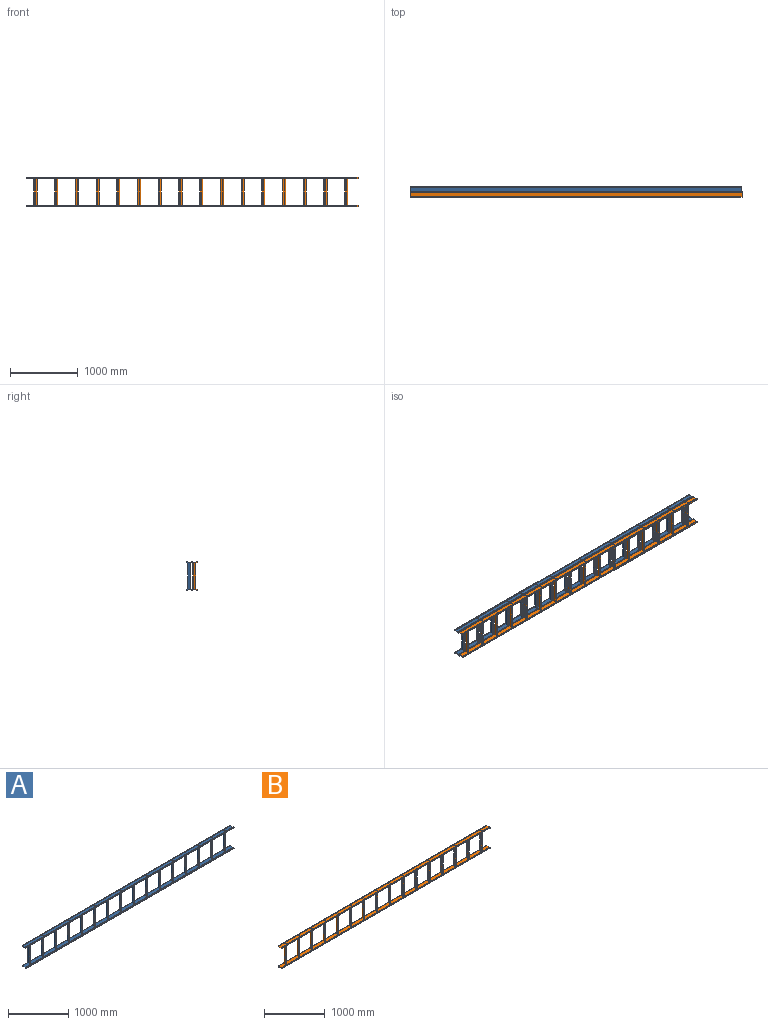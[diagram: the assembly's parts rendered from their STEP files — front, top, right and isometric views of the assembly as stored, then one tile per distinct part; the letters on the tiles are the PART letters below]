
ASSEMBLY  parts=2 mates=1
PART A: 108 faces, bbox 4876.8x88.6x440.7 mm
  f0: plane 4876.8x69.85mm, normal (0,0,1), area 321795mm2, adj f17,f18,f20,f42,f43,f44,f45,f46
  f1: plane 4876.8x22.23mm, normal (0,-1,0), area 108386.9mm2, adj f2,f19,f20,f102
  f2: plane 4876.8x7.46mm, normal (0,0,1), area 36387mm2, adj f1,f3,f20,f102
  f3: plane 4876.8x3.97mm, normal (0,1,0), area 19354.8mm2, adj f2,f4,f20,f102
  f4: plane 4876.8x3.18mm, normal (0,0,-1), area 15483.8mm2, adj f3,f5,f20,f102
  f5: plane 4876.8x2.38mm, normal (0,1,0), area 11612.9mm2, adj f4,f6,f20,f102
  f6: plane 4876.8x5.56mm, normal (0,0,1), area 27096.7mm2, adj f5,f7,f20,f102
  f7: plane 4876.8x10.8mm, normal (0,-1,0), area 52645.1mm2, adj f6,f8,f20,f102
  f8: plane 4876.8x14.29mm, normal (0,0,-1), area 69677.3mm2, adj f7,f9,f20,f102
  f9: plane 4876.8x16.72mm, normal (0,1,0), area 81548.1mm2, adj f8,f10,f20,f102
  f10: plane 4876.8x69.85mm, normal (0,0,-1), area 340644.5mm2, adj f9,f11,f20,f102
  f11: plane 4876.8x9.1mm, normal (0,-1,0), area 44386.8mm2, adj f10,f12,f20,f102
  f12: plane 4876.8x2.38mm, normal (0,0,1), area 11612.9mm2, adj f11,f13,f20,f102
  f13: plane 4876.8x3.18mm, normal (0,-1,0), area 15483.8mm2, adj f12,f14,f20,f102
  f14: plane 4876.8x6.83mm, normal (0,0,-1), area 33290.3mm2, adj f13,f15,f20,f102
  f15: plane 4876.8x22.23mm, normal (0,1,0), area 108386.9mm2, adj f14,f16,f20,f102
  f16: plane 4876.8x4.45mm, normal (0,0,1), area 21677.4mm2, adj f15,f17,f20,f102
  f17: plane 4876.8x3.18mm, normal (0,-1,0), area 15483.8mm2, adj f0,f16,f20,f102
  f18: plane 4876.8x3.18mm, normal (0,1,0), area 15483.8mm2, adj f0,f19,f20,f102
  f19: plane 4876.8x4.45mm, normal (0,0,1), area 21677.4mm2, adj f1,f18,f20,f102
  f20: plane 88.58x26.67mm, normal (-1,0,0), area 764.4mm2, adj f0,f1,f2,f3,f4,f5,f6,f7
  f21: plane 4876.8x69.85mm, normal (0,0,-1), area 321795mm2, adj f33,f34,f41,f42,f43,f44,f45,f46
  f22: plane 4876.8x69.85mm, normal (0,0,1), area 340644.5mm2, adj f23,f40,f41,f103
  f23: plane 4876.8x16.72mm, normal (0,1,0), area 81548.1mm2, adj f22,f24,f41,f103
  f24: plane 4876.8x14.29mm, normal (0,0,1), area 69677.3mm2, adj f23,f25,f41,f103
  f25: plane 4876.8x10.8mm, normal (0,-1,0), area 52645.1mm2, adj f24,f26,f41,f103
  f26: plane 4876.8x5.56mm, normal (0,0,-1), area 27096.7mm2, adj f25,f27,f41,f103
  f27: plane 4876.8x2.38mm, normal (0,1,0), area 11612.9mm2, adj f26,f28,f41,f103
  f28: plane 4876.8x3.18mm, normal (0,0,1), area 15483.8mm2, adj f27,f29,f41,f103
  f29: plane 4876.8x3.97mm, normal (0,1,0), area 19354.8mm2, adj f28,f30,f41,f103
  f30: plane 4876.8x7.46mm, normal (0,0,-1), area 36387mm2, adj f29,f31,f41,f103
  f31: plane 4876.8x22.23mm, normal (0,-1,0), area 108386.9mm2, adj f30,f32,f41,f103
  f32: plane 4876.8x4.45mm, normal (0,0,-1), area 21677.4mm2, adj f31,f33,f41,f103
  f33: plane 4876.8x3.18mm, normal (0,1,0), area 15483.8mm2, adj f21,f32,f41,f103
  f34: plane 4876.8x3.18mm, normal (0,-1,0), area 15483.8mm2, adj f21,f35,f41,f103
  f35: plane 4876.8x4.45mm, normal (0,0,-1), area 21677.4mm2, adj f34,f36,f41,f103
  f36: plane 4876.8x22.23mm, normal (0,1,0), area 108386.9mm2, adj f35,f37,f41,f103
  f37: plane 4876.8x6.83mm, normal (0,0,1), area 33290.3mm2, adj f36,f38,f41,f103
  f38: plane 4876.8x3.18mm, normal (0,-1,0), area 15483.8mm2, adj f37,f39,f41,f103
  f39: plane 4876.8x2.38mm, normal (0,0,-1), area 11612.9mm2, adj f38,f40,f41,f103
  f40: plane 4876.8x9.1mm, normal (0,-1,0), area 44386.8mm2, adj f22,f39,f41,f103
  f41: plane 88.58x26.67mm, normal (-1,0,0), area 764.4mm2, adj f21,f22,f23,f24,f25,f26,f27,f28
  f42: plane 393.7x18.97mm, normal (0,-1,0), area 7469.5mm2, adj f0,f21,f43,f44
  f43: plane 393.7x43.18mm, normal (-0.97,0.26,0), area 17599.7mm2, adj f0,f21,f42,f45
  f44: cylinder r=17.46mm len=393.7mm, axis (0,0,-1), area 20918.1mm2, adj f0,f21,f42,f45
  f45: plane 393.7x16.43mm, normal (0.5,0.87,0), area 7469.5mm2, adj f0,f21,f43,f44
  f46: plane 393.7x18.97mm, normal (0,-1,0), area 7469.5mm2, adj f0,f21,f47,f48
  f47: plane 393.7x43.18mm, normal (-0.97,0.26,0), area 17599.7mm2, adj f0,f21,f46,f49
  f48: cylinder r=17.46mm len=393.7mm, axis (0,0,-1), area 20918.1mm2, adj f0,f21,f46,f49
  f49: plane 393.7x16.43mm, normal (0.5,0.87,0), area 7469.5mm2, adj f0,f21,f47,f48
  f50: plane 393.7x18.97mm, normal (0,-1,0), area 7469.5mm2, adj f0,f21,f51,f52
  f51: plane 393.7x43.18mm, normal (-0.97,0.26,0), area 17599.7mm2, adj f0,f21,f50,f53
  f52: cylinder r=17.46mm len=393.7mm, axis (0,0,-1), area 20918.1mm2, adj f0,f21,f50,f53
  f53: plane 393.7x16.43mm, normal (0.5,0.87,0), area 7469.5mm2, adj f0,f21,f51,f52
  f54: plane 393.7x18.97mm, normal (0,-1,0), area 7469.5mm2, adj f0,f21,f55,f56
  f55: plane 393.7x43.18mm, normal (-0.97,0.26,0), area 17599.7mm2, adj f0,f21,f54,f57
  f56: cylinder r=17.46mm len=393.7mm, axis (0,0,-1), area 20918.1mm2, adj f0,f21,f54,f57
  f57: plane 393.7x16.43mm, normal (0.5,0.87,0), area 7469.5mm2, adj f0,f21,f55,f56
  f58: plane 393.7x18.97mm, normal (0,-1,0), area 7469.5mm2, adj f0,f21,f59,f60
  f59: plane 393.7x43.18mm, normal (-0.97,0.26,0), area 17599.7mm2, adj f0,f21,f58,f61
  f60: cylinder r=17.46mm len=393.7mm, axis (0,0,-1), area 20918.1mm2, adj f0,f21,f58,f61
  f61: plane 393.7x16.43mm, normal (0.5,0.87,0), area 7469.5mm2, adj f0,f21,f59,f60
  f62: plane 393.7x18.97mm, normal (0,-1,0), area 7469.5mm2, adj f0,f21,f63,f64
  f63: plane 393.7x43.18mm, normal (-0.97,0.26,0), area 17599.7mm2, adj f0,f21,f62,f65
  f64: cylinder r=17.46mm len=393.7mm, axis (0,0,-1), area 20918.1mm2, adj f0,f21,f62,f65
  f65: plane 393.7x16.43mm, normal (0.5,0.87,0), area 7469.5mm2, adj f0,f21,f63,f64
  f66: plane 393.7x18.97mm, normal (0,-1,0), area 7469.5mm2, adj f0,f21,f67,f68
  f67: plane 393.7x43.18mm, normal (-0.97,0.26,0), area 17599.7mm2, adj f0,f21,f66,f69
  f68: cylinder r=17.46mm len=393.7mm, axis (0,0,-1), area 20918.1mm2, adj f0,f21,f66,f69
  f69: plane 393.7x16.43mm, normal (0.5,0.87,0), area 7469.5mm2, adj f0,f21,f67,f68
  f70: plane 393.7x18.97mm, normal (0,-1,0), area 7469.5mm2, adj f0,f21,f71,f72
  f71: plane 393.7x43.18mm, normal (-0.97,0.26,0), area 17599.7mm2, adj f0,f21,f70,f73
  f72: cylinder r=17.46mm len=393.7mm, axis (0,0,-1), area 20918.1mm2, adj f0,f21,f70,f73
  f73: plane 393.7x16.43mm, normal (0.5,0.87,0), area 7469.5mm2, adj f0,f21,f71,f72
  f74: plane 393.7x18.97mm, normal (0,-1,0), area 7469.5mm2, adj f0,f21,f75,f76
  f75: plane 393.7x43.18mm, normal (-0.97,0.26,0), area 17599.7mm2, adj f0,f21,f74,f77
  f76: cylinder r=17.46mm len=393.7mm, axis (0,0,-1), area 20918.1mm2, adj f0,f21,f74,f77
  f77: plane 393.7x16.43mm, normal (0.5,0.87,0), area 7469.5mm2, adj f0,f21,f75,f76
  f78: plane 393.7x18.97mm, normal (0,-1,0), area 7469.5mm2, adj f0,f21,f79,f80
  f79: plane 393.7x43.18mm, normal (-0.97,0.26,0), area 17599.7mm2, adj f0,f21,f78,f81
  f80: cylinder r=17.46mm len=393.7mm, axis (0,0,-1), area 20918.1mm2, adj f0,f21,f78,f81
  f81: plane 393.7x16.43mm, normal (0.5,0.87,0), area 7469.5mm2, adj f0,f21,f79,f80
  f82: plane 393.7x18.97mm, normal (0,-1,0), area 7469.5mm2, adj f0,f21,f83,f84
  f83: plane 393.7x43.18mm, normal (-0.97,0.26,0), area 17599.7mm2, adj f0,f21,f82,f85
  f84: cylinder r=17.46mm len=393.7mm, axis (0,0,-1), area 20918.1mm2, adj f0,f21,f82,f85
  f85: plane 393.7x16.43mm, normal (0.5,0.87,0), area 7469.5mm2, adj f0,f21,f83,f84
  f86: plane 393.7x18.97mm, normal (0,-1,0), area 7469.5mm2, adj f0,f21,f87,f88
  f87: plane 393.7x43.18mm, normal (-0.97,0.26,0), area 17599.7mm2, adj f0,f21,f86,f89
  f88: cylinder r=17.46mm len=393.7mm, axis (0,0,-1), area 20918.1mm2, adj f0,f21,f86,f89
  f89: plane 393.7x16.43mm, normal (0.5,0.87,0), area 7469.5mm2, adj f0,f21,f87,f88
  f90: plane 393.7x18.97mm, normal (0,-1,0), area 7469.5mm2, adj f0,f21,f91,f92
  f91: plane 393.7x43.18mm, normal (-0.97,0.26,0), area 17599.7mm2, adj f0,f21,f90,f93
  f92: cylinder r=17.46mm len=393.7mm, axis (0,0,-1), area 20918.1mm2, adj f0,f21,f90,f93
  f93: plane 393.7x16.43mm, normal (0.5,0.87,0), area 7469.5mm2, adj f0,f21,f91,f92
  f94: plane 393.7x18.97mm, normal (0,-1,0), area 7469.5mm2, adj f0,f21,f95,f96
  f95: plane 393.7x43.18mm, normal (-0.97,0.26,0), area 17599.7mm2, adj f0,f21,f94,f97
  f96: cylinder r=17.46mm len=393.7mm, axis (0,0,-1), area 20918.1mm2, adj f0,f21,f94,f97
  f97: plane 393.7x16.43mm, normal (0.5,0.87,0), area 7469.5mm2, adj f0,f21,f95,f96
  f98: plane 393.7x18.97mm, normal (0,-1,0), area 7469.5mm2, adj f0,f21,f99,f100
  f99: plane 393.7x43.18mm, normal (-0.97,0.26,0), area 17599.7mm2, adj f0,f21,f98,f101
  f100: cylinder r=17.46mm len=393.7mm, axis (0,0,-1), area 20918.1mm2, adj f0,f21,f98,f101
  f101: plane 393.7x16.43mm, normal (0.5,0.87,0), area 7469.5mm2, adj f0,f21,f99,f100
  f102: plane 88.58x26.67mm, normal (1,0,0), area 764.4mm2, adj f0,f1,f2,f3,f4,f5,f6,f7
  f103: plane 88.58x26.67mm, normal (1,0,0), area 764.4mm2, adj f21,f22,f23,f24,f25,f26,f27,f28
  f104: plane 393.7x18.97mm, normal (0,-1,0), area 7469.5mm2, adj f0,f21,f105,f106
  f105: plane 393.7x43.18mm, normal (-0.97,0.26,0), area 17599.7mm2, adj f0,f21,f104,f107
  f106: cylinder r=17.46mm len=393.7mm, axis (0,0,-1), area 20918.1mm2, adj f0,f21,f104,f107
  f107: plane 393.7x16.43mm, normal (0.5,0.87,0), area 7469.5mm2, adj f0,f21,f105,f106
PART B: 100 faces, bbox 4876.8x78.7x431.8 mm
  f0: plane 4876.8x69.85mm, normal (0,0,1), area 321795mm2, adj f12,f13,f16,f34,f35,f36,f37,f38
  f1: plane 4876.8x7.62mm, normal (0,0,-1), area 37161.2mm2, adj f2,f15,f16,f94
  f2: plane 4876.8x3.18mm, normal (0,1,0), area 15483.8mm2, adj f1,f3,f16,f94
  f3: plane 4876.8x3.18mm, normal (0,0,1), area 15483.8mm2, adj f2,f4,f16,f94
  f4: plane 4876.8x9.1mm, normal (0,1,0), area 44386.8mm2, adj f3,f5,f16,f94
  f5: plane 4876.8x69.85mm, normal (0,0,-1), area 340644.5mm2, adj f4,f6,f16,f94
  f6: plane 4876.8x9.1mm, normal (0,-1,0), area 44386.8mm2, adj f5,f7,f16,f94
  f7: plane 4876.8x3.18mm, normal (0,0,1), area 15483.8mm2, adj f6,f8,f16,f94
  f8: plane 4876.8x3.18mm, normal (0,-1,0), area 15483.8mm2, adj f7,f9,f16,f94
  f9: plane 4876.8x7.62mm, normal (0,0,-1), area 37161.2mm2, adj f8,f10,f16,f94
  f10: plane 4876.8x22.23mm, normal (0,1,0), area 108386.9mm2, adj f9,f11,f16,f94
  f11: plane 4876.8x4.45mm, normal (0,0,1), area 21677.4mm2, adj f10,f12,f16,f94
  f12: plane 4876.8x3.18mm, normal (0,-1,0), area 15483.8mm2, adj f0,f11,f16,f94
  f13: plane 4876.8x3.18mm, normal (0,1,0), area 15483.8mm2, adj f0,f14,f16,f94
  f14: plane 4876.8x4.45mm, normal (0,0,1), area 21677.4mm2, adj f13,f15,f16,f94
  f15: plane 4876.8x22.23mm, normal (0,-1,0), area 108386.9mm2, adj f1,f14,f16,f94
  f16: plane 78.74x22.23mm, normal (-1,0,0), area 690.9mm2, adj f0,f1,f2,f3,f4,f5,f6,f7
  f17: plane 4876.8x69.85mm, normal (0,0,-1), area 321795mm2, adj f25,f26,f33,f34,f35,f36,f37,f38
  f18: plane 4876.8x69.85mm, normal (0,0,1), area 340644.5mm2, adj f19,f32,f33,f95
  f19: plane 4876.8x9.1mm, normal (0,1,0), area 44386.8mm2, adj f18,f20,f33,f95
  f20: plane 4876.8x3.18mm, normal (0,0,-1), area 15483.8mm2, adj f19,f21,f33,f95
  f21: plane 4876.8x3.18mm, normal (0,1,0), area 15483.8mm2, adj f20,f22,f33,f95
  f22: plane 4876.8x7.62mm, normal (0,0,1), area 37161.2mm2, adj f21,f23,f33,f95
  f23: plane 4876.8x22.23mm, normal (0,-1,0), area 108386.9mm2, adj f22,f24,f33,f95
  f24: plane 4876.8x4.45mm, normal (0,0,-1), area 21677.4mm2, adj f23,f25,f33,f95
  f25: plane 4876.8x3.18mm, normal (0,1,0), area 15483.8mm2, adj f17,f24,f33,f95
  f26: plane 4876.8x3.18mm, normal (0,-1,0), area 15483.8mm2, adj f17,f27,f33,f95
  f27: plane 4876.8x4.45mm, normal (0,0,-1), area 21677.4mm2, adj f26,f28,f33,f95
  f28: plane 4876.8x22.23mm, normal (0,1,0), area 108386.9mm2, adj f27,f29,f33,f95
  f29: plane 4876.8x7.62mm, normal (0,0,1), area 37161.2mm2, adj f28,f30,f33,f95
  f30: plane 4876.8x3.18mm, normal (0,-1,0), area 15483.8mm2, adj f29,f31,f33,f95
  f31: plane 4876.8x3.18mm, normal (0,0,-1), area 15483.8mm2, adj f30,f32,f33,f95
  f32: plane 4876.8x9.1mm, normal (0,-1,0), area 44386.8mm2, adj f18,f31,f33,f95
  f33: plane 78.74x22.23mm, normal (-1,0,0), area 690.9mm2, adj f17,f18,f19,f20,f21,f22,f23,f24
  f34: plane 393.7x18.97mm, normal (0,-1,0), area 7469.5mm2, adj f0,f17,f35,f36
  f35: plane 393.7x43.18mm, normal (-0.97,0.26,0), area 17599.7mm2, adj f0,f17,f34,f37
  f36: cylinder r=17.46mm len=393.7mm, axis (0,0,-1), area 20918.1mm2, adj f0,f17,f34,f37
  f37: plane 393.7x16.43mm, normal (0.5,0.87,0), area 7469.5mm2, adj f0,f17,f35,f36
  f38: plane 393.7x18.97mm, normal (0,-1,0), area 7469.5mm2, adj f0,f17,f39,f40
  f39: plane 393.7x43.18mm, normal (-0.97,0.26,0), area 17599.7mm2, adj f0,f17,f38,f41
  f40: cylinder r=17.46mm len=393.7mm, axis (0,0,-1), area 20918.1mm2, adj f0,f17,f38,f41
  f41: plane 393.7x16.43mm, normal (0.5,0.87,0), area 7469.5mm2, adj f0,f17,f39,f40
  f42: plane 393.7x18.97mm, normal (0,-1,0), area 7469.5mm2, adj f0,f17,f43,f44
  f43: plane 393.7x43.18mm, normal (-0.97,0.26,0), area 17599.7mm2, adj f0,f17,f42,f45
  f44: cylinder r=17.46mm len=393.7mm, axis (0,0,-1), area 20918.1mm2, adj f0,f17,f42,f45
  f45: plane 393.7x16.43mm, normal (0.5,0.87,0), area 7469.5mm2, adj f0,f17,f43,f44
  f46: plane 393.7x18.97mm, normal (0,-1,0), area 7469.5mm2, adj f0,f17,f47,f48
  f47: plane 393.7x43.18mm, normal (-0.97,0.26,0), area 17599.7mm2, adj f0,f17,f46,f49
  f48: cylinder r=17.46mm len=393.7mm, axis (0,0,-1), area 20918.1mm2, adj f0,f17,f46,f49
  f49: plane 393.7x16.43mm, normal (0.5,0.87,0), area 7469.5mm2, adj f0,f17,f47,f48
  f50: plane 393.7x18.97mm, normal (0,-1,0), area 7469.5mm2, adj f0,f17,f51,f52
  f51: plane 393.7x43.18mm, normal (-0.97,0.26,0), area 17599.7mm2, adj f0,f17,f50,f53
  f52: cylinder r=17.46mm len=393.7mm, axis (0,0,-1), area 20918.1mm2, adj f0,f17,f50,f53
  f53: plane 393.7x16.43mm, normal (0.5,0.87,0), area 7469.5mm2, adj f0,f17,f51,f52
  f54: plane 393.7x18.97mm, normal (0,-1,0), area 7469.5mm2, adj f0,f17,f55,f56
  f55: plane 393.7x43.18mm, normal (-0.97,0.26,0), area 17599.7mm2, adj f0,f17,f54,f57
  f56: cylinder r=17.46mm len=393.7mm, axis (0,0,-1), area 20918.1mm2, adj f0,f17,f54,f57
  f57: plane 393.7x16.43mm, normal (0.5,0.87,0), area 7469.5mm2, adj f0,f17,f55,f56
  f58: plane 393.7x18.97mm, normal (0,-1,0), area 7469.5mm2, adj f0,f17,f59,f60
  f59: plane 393.7x43.18mm, normal (-0.97,0.26,0), area 17599.7mm2, adj f0,f17,f58,f61
  f60: cylinder r=17.46mm len=393.7mm, axis (0,0,-1), area 20918.1mm2, adj f0,f17,f58,f61
  f61: plane 393.7x16.43mm, normal (0.5,0.87,0), area 7469.5mm2, adj f0,f17,f59,f60
  f62: plane 393.7x18.97mm, normal (0,-1,0), area 7469.5mm2, adj f0,f17,f63,f64
  f63: plane 393.7x43.18mm, normal (-0.97,0.26,0), area 17599.7mm2, adj f0,f17,f62,f65
  f64: cylinder r=17.46mm len=393.7mm, axis (0,0,-1), area 20918.1mm2, adj f0,f17,f62,f65
  f65: plane 393.7x16.43mm, normal (0.5,0.87,0), area 7469.5mm2, adj f0,f17,f63,f64
  f66: plane 393.7x18.97mm, normal (0,-1,0), area 7469.5mm2, adj f0,f17,f67,f68
  f67: plane 393.7x43.18mm, normal (-0.97,0.26,0), area 17599.7mm2, adj f0,f17,f66,f69
  f68: cylinder r=17.46mm len=393.7mm, axis (0,0,-1), area 20918.1mm2, adj f0,f17,f66,f69
  f69: plane 393.7x16.43mm, normal (0.5,0.87,0), area 7469.5mm2, adj f0,f17,f67,f68
  f70: plane 393.7x18.97mm, normal (0,-1,0), area 7469.5mm2, adj f0,f17,f71,f72
  f71: plane 393.7x43.18mm, normal (-0.97,0.26,0), area 17599.7mm2, adj f0,f17,f70,f73
  f72: cylinder r=17.46mm len=393.7mm, axis (0,0,-1), area 20918.1mm2, adj f0,f17,f70,f73
  f73: plane 393.7x16.43mm, normal (0.5,0.87,0), area 7469.5mm2, adj f0,f17,f71,f72
  f74: plane 393.7x18.97mm, normal (0,-1,0), area 7469.5mm2, adj f0,f17,f75,f76
  f75: plane 393.7x43.18mm, normal (-0.97,0.26,0), area 17599.7mm2, adj f0,f17,f74,f77
  f76: cylinder r=17.46mm len=393.7mm, axis (0,0,-1), area 20918.1mm2, adj f0,f17,f74,f77
  f77: plane 393.7x16.43mm, normal (0.5,0.87,0), area 7469.5mm2, adj f0,f17,f75,f76
  f78: plane 393.7x18.97mm, normal (0,-1,0), area 7469.5mm2, adj f0,f17,f79,f80
  f79: plane 393.7x43.18mm, normal (-0.97,0.26,0), area 17599.7mm2, adj f0,f17,f78,f81
  f80: cylinder r=17.46mm len=393.7mm, axis (0,0,-1), area 20918.1mm2, adj f0,f17,f78,f81
  f81: plane 393.7x16.43mm, normal (0.5,0.87,0), area 7469.5mm2, adj f0,f17,f79,f80
  f82: plane 393.7x18.97mm, normal (0,-1,0), area 7469.5mm2, adj f0,f17,f83,f84
  f83: plane 393.7x43.18mm, normal (-0.97,0.26,0), area 17599.7mm2, adj f0,f17,f82,f85
  f84: cylinder r=17.46mm len=393.7mm, axis (0,0,-1), area 20918.1mm2, adj f0,f17,f82,f85
  f85: plane 393.7x16.43mm, normal (0.5,0.87,0), area 7469.5mm2, adj f0,f17,f83,f84
  f86: plane 393.7x18.97mm, normal (0,-1,0), area 7469.5mm2, adj f0,f17,f87,f88
  f87: plane 393.7x43.18mm, normal (-0.97,0.26,0), area 17599.7mm2, adj f0,f17,f86,f89
  f88: cylinder r=17.46mm len=393.7mm, axis (0,0,-1), area 20918.1mm2, adj f0,f17,f86,f89
  f89: plane 393.7x16.43mm, normal (0.5,0.87,0), area 7469.5mm2, adj f0,f17,f87,f88
  f90: plane 393.7x18.97mm, normal (0,-1,0), area 7469.5mm2, adj f0,f17,f91,f92
  f91: plane 393.7x43.18mm, normal (-0.97,0.26,0), area 17599.7mm2, adj f0,f17,f90,f93
  f92: cylinder r=17.46mm len=393.7mm, axis (0,0,-1), area 20918.1mm2, adj f0,f17,f90,f93
  f93: plane 393.7x16.43mm, normal (0.5,0.87,0), area 7469.5mm2, adj f0,f17,f91,f92
  f94: plane 78.74x22.23mm, normal (1,0,0), area 690.9mm2, adj f0,f1,f2,f3,f4,f5,f6,f7
  f95: plane 78.74x22.23mm, normal (1,0,0), area 690.9mm2, adj f17,f18,f19,f20,f21,f22,f23,f24
  f96: plane 393.7x18.97mm, normal (0,-1,0), area 7469.5mm2, adj f0,f17,f97,f98
  f97: plane 393.7x43.18mm, normal (-0.97,0.26,0), area 17599.7mm2, adj f0,f17,f96,f99
  f98: cylinder r=17.46mm len=393.7mm, axis (0,0,-1), area 20918.1mm2, adj f0,f17,f96,f99
  f99: plane 393.7x16.43mm, normal (0.5,0.87,0), area 7469.5mm2, adj f0,f17,f97,f98
PLACE A t=(-57.15,272.98,0)mm
PLACE B t=(-50.8,194.32,0)mm
MATE planar A.f30 <-> B.f29  axis (0,0,-1) through (2076.45,229.88,412.75)mm
